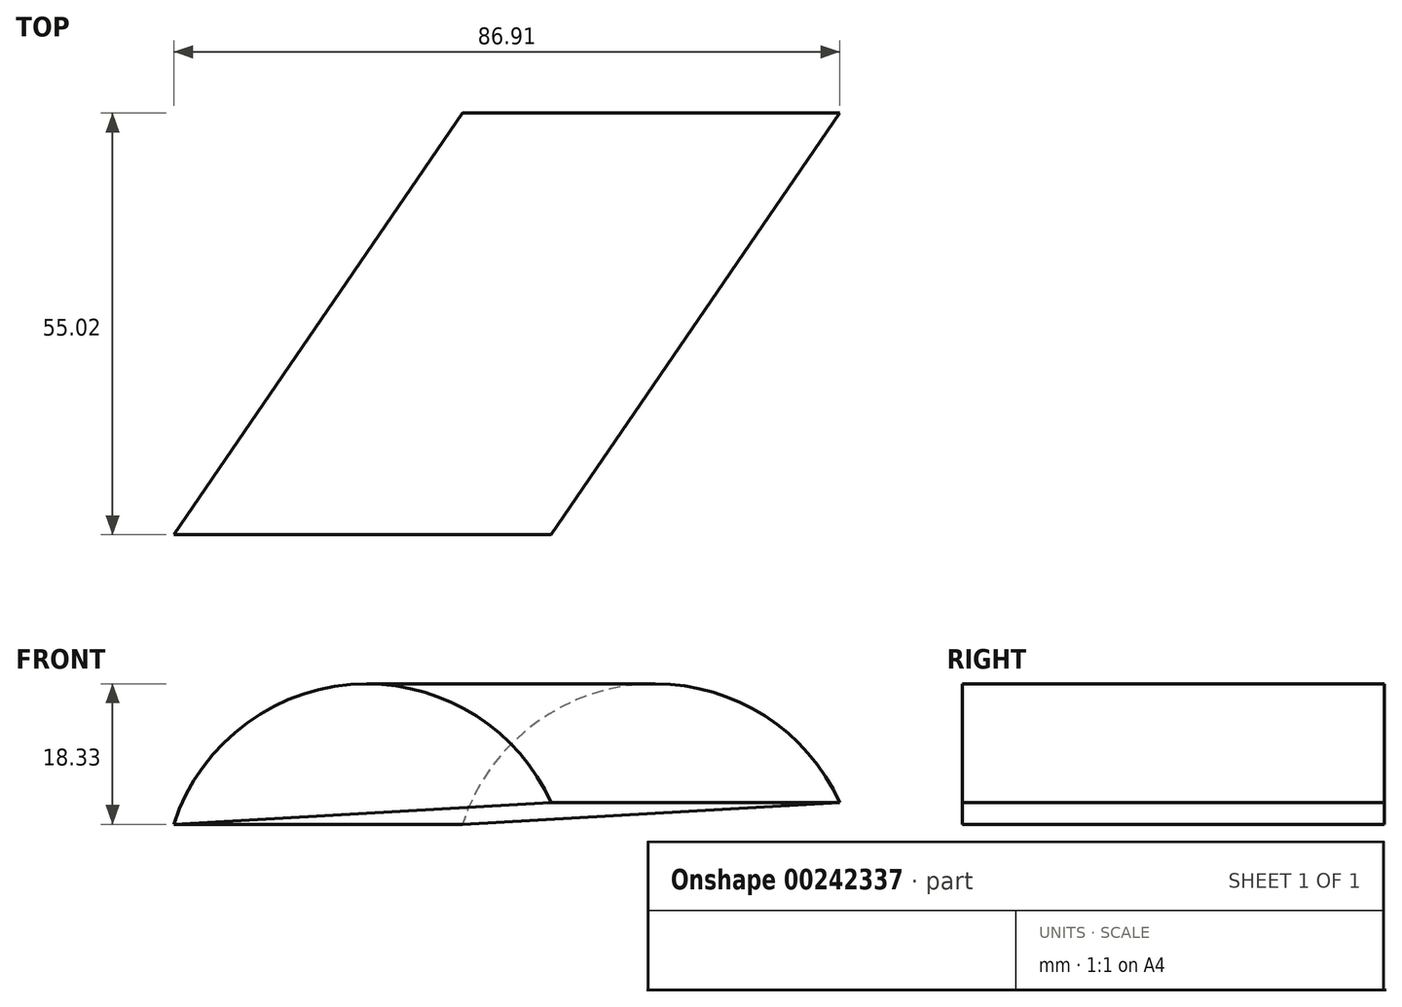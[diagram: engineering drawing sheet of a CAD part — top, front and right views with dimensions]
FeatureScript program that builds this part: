
annotation { "Feature Type Name" : "Feature", "Feature Type Description" : "" }
export const myFeature = defineFeature(function(context is Context, id is Id, definition is map)
    precondition{}
    {
        {
            var Q0;
            Q0=qCreatedBy(makeId("Front.planeOp"),FACE);
            var sketch = newSketch(context, id + "F0", { "sketchPlane" : qUnion([Q0])});
            skLineSegment(sketch, "E0", {"start": v(0, 0) * mm, "end": v(-49.25, -2.85) * mm});
            skArc(sketch, "E1", {"start": v(0, 0) * mm, "mid": v(-25.6, 15.44) * mm, "end": v(-49.25, -2.85) * mm});
            skSolve(sketch);
        }
        {
            var Q0;
            Q0=qCreatedBy(makeId("Top.planeOp"),FACE);
            var sketch = newSketch(context, id + "F1", { "sketchPlane" : qUnion([Q0])});
            skLineSegment(sketch, "E2", {"start": v(0, 0) * mm, "end": v(-37.65, -55.02) * mm});
            skSolve(sketch);
        }
        {
            var Q0;
            Q0=makeQuery(id+"F0.imprint","IMPRINT",FACE,{"disambiguationData":[TD([[makeQuery(id+"F0.imprint","IMPRINT",EDGE,{"derivedFrom":sQuery(id+"F0.wireOp",EDGE,"E0")}),-1.0]])]});
            var Q1;
            Q1=sQuery(id+"F1.wireOp",EDGE,"E2");
            sweep(context, id + "F2", {"profiles" : qUnion([Q0]), "path" : qUnion([Q1])});
        }
    });
